FCSTD DOCUMENT  (FreeCAD 1.0RUnknown)
Label: arc
License: All rights reserved
LicenseURL: http://en.wikipedia.org/wiki/All_rights_reserved
objects: Sketcher::SketchObject×1, PartDesign::Body×1
note: 3 computed .brp shape members not serialized (recipe doc carries the construction recipe); baked Part::Feature solids carry a one-line shape summary decoded from their .brp

FEATURE [Sketcher::SketchObject] Sketch
  ArcFitTolerance = 1e-06
  AttachmentSupport = -> [XY_Plane]
  FullyConstrained = true
  MakeInternals = false
  MapMode = 5
  sketch-geometry (10):
    g0: LineSegment StartX=5.18748 StartY=-1.8e-15 StartZ=0 EndX=15 EndY=6 EndZ=0
    g1: ArcOfCircle CenterX=12.3917 CenterY=10.2657 CenterZ=0 NormalX=0 NormalY=0 NormalZ=1 AngleXU=0 Radius=5 StartAngle=5.2612 EndAngle=7.52649
    g2: ArcOfCircle CenterX=10.2126 CenterY=16.2867 CenterZ=0 NormalX=0 NormalY=0 NormalZ=1 AngleXU=0 Radius=4 StartAngle=4.12625 EndAngle=5.95569
    g3: LineSegment StartX=4 StartY=17 StartZ=0 EndX=-4 EndY=17 EndZ=0
    g4: ArcOfCircle CenterX=-4 CenterY=6.01736 CenterZ=0 NormalX=0 NormalY=0 NormalZ=1 AngleXU=0 Radius=10.9826 StartAngle=1.5708 EndAngle=5.70334
    g5: ArcOfCircle CenterX=10.2126 CenterY=16.2867 CenterZ=0 NormalX=0 NormalY=0 NormalZ=1 AngleXU=0 Radius=4 StartAngle=3.21332 EndAngle=4.12625
    g6: LineSegment StartX=6.22288 StartY=16 StartZ=0 EndX=4 EndY=17 EndZ=0
    g7: GeomPoint X=17.3917 Y=10.2657 Z=0
    g8: LineSegment [constr] StartX=17.3917 StartY=10.2657 StartZ=0 EndX=17.3917 EndY=0 EndZ=0
    g9: LineSegment [constr] StartX=-14.9826 StartY=6.01736 StartZ=0 EndX=-14.9826 EndY=0 EndZ=0
  constraints (37):
    c: Tangent(g0,g1) = -1.5708
    c: Perpendicular(g1,g2) = 4.71239
    c: Horizontal(g3)
    c: Tangent(g3,g4) = -1.5708
    c: Coincident(g4,g0)
    c: Coincident(g5,g2)
    c: Coincident(g5,g2)
    c: Coincident(g6,g5)
    c: Coincident(g6,g3)
    c: DistanceX(g0) = 15
    c: DistanceY(g0) = 6
    c: DistanceX(g1) = 14
    c: DistanceY(g1) = 15
    c: DistanceX(g5) = 6.22288
    c: DistanceY(g5) = 16
    c: DistanceX(g3) = 4
    c: DistanceY(g3) = 17
    c: DistanceX(g3) = -4
    c: Radius(g1) = 5
    c: PointOnObject(g0,g-1)
    c: DistanceX(g2) = 8
    c: DistanceX(g-1,g0) = 5.18748
    c: DistanceY(g2) = 12.9543
    c: Radius(g4) = 10.9826
    c: Radius(g2) = 4
    c: PointOnObject(g7,g1)
    c: Coincident(g8,g7)
    c: PointOnObject(g8,g-1)
    c: Vertical(g8)
    c: Tangent(g8,g1)
    c: DistanceX(g7) = 17.3917
    c: DistanceY(g-1,g7) = 10.2657
    c: Tangent(g9,g4) = -1.5708
    c: PointOnObject(g9,g-1)
    c: Vertical(g9)
    c: DistanceY(g9) = 6.01736
    c: DistanceX(g9,g-1) = 14.9826
FEATURE [PartDesign::Body] Body
  AllowCompound = false
  Group = -> [Sketch]
  Origin = -> Origin
